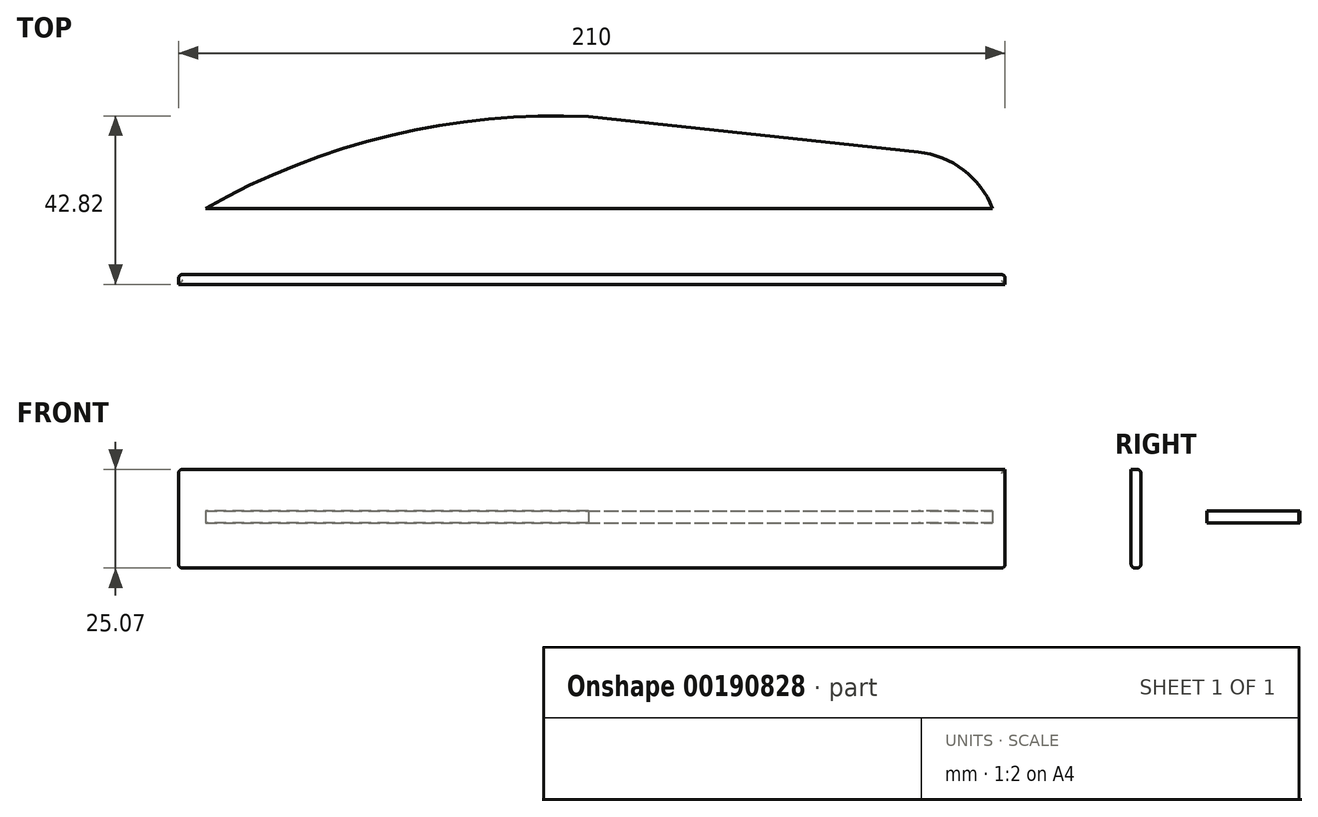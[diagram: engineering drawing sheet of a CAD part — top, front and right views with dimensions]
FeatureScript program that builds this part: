
annotation { "Feature Type Name" : "Feature", "Feature Type Description" : "" }
export const myFeature = defineFeature(function(context is Context, id is Id, definition is map)
    precondition{}
    {
        {
            var Q0;
            Q0=qCreatedBy(makeId("Top.planeOp"),FACE);
            var sketch = newSketch(context, id + "F0", { "sketchPlane" : qUnion([Q0])});
            skLineSegment(sketch, "E0", {"start": v(-82.54, 16.8) * mm, "end": v(117.46, 16.8) * mm});
            skArc(sketch, "E1", {"start": v(14.74, 40.14) * mm, "mid": v(-35.55, 35.33) * mm, "end": v(-82.54, 16.8) * mm});
            skLineSegment(sketch, "E2", {"start": v(14.74, 40.14) * mm, "end": v(98.58, 31.13) * mm});
            skArc(sketch, "E3", {"start": v(117.46, 16.8) * mm, "mid": v(110.01, 26.59) * mm, "end": v(98.58, 31.13) * mm});
            skSolve(sketch);
        }
        {
            var Q0;
            Q0=makeQuery(id+"F0.imprint","IMPRINT",FACE,{"disambiguationData":[TD([[makeQuery(id+"F0.imprint","IMPRINT",EDGE,{"derivedFrom":sQuery(id+"F0.wireOp",EDGE,"E0")}),1.0]])]});
            extrude(context, id + "F1", {"entities" : qUnion([Q0]), "depth" : 3 * mm});
        }
        {
            var Q0;
            Q0=qCreatedBy(makeId("Front.planeOp"),FACE);
            var sketch = newSketch(context, id + "F2", { "sketchPlane" : qUnion([Q0])});
            skLineSegment(sketch, "E4.bottom", {"start": v(-89.37, 13.57) * mm, "end": v(120.63, 13.57) * mm});
            skLineSegment(sketch, "E4.top", {"start": v(-89.37, -11.5) * mm, "end": v(120.63, -11.5) * mm});
            skLineSegment(sketch, "E4.left", {"start": v(-89.37, 13.57) * mm, "end": v(-89.37, -11.5) * mm});
            skLineSegment(sketch, "E4.right", {"start": v(120.63, 13.57) * mm, "end": v(120.63, -11.5) * mm});
            skSolve(sketch);
        }
        {
            var Q0;
            Q0=makeQuery(id+"F2.imprint","IMPRINT",FACE,{"disambiguationData":[TD([[makeQuery(id+"F2.imprint","IMPRINT",EDGE,{"derivedFrom":sQuery(id+"F2.wireOp",EDGE,"E4.bottom")}),-1.0]])]});
            extrude(context, id + "F3", {"entities" : qUnion([Q0]), "depth" : 2.5 * mm});
        }
        {
            var Q0;
            Q0=makeQuery(id+"F3.opExtrude","SWEPT_EDGE",EDGE,{"disambiguationData":[OSD([sQuery(id+"F2.wireOp",EDGE,"E4.bottom"),sQuery(id+"F2.wireOp",EDGE,"E4.left")])]});
            var Q1;
            Q1=makeQuery(id+"F3.opExtrude","CAP_EDGE",EDGE,{"disambiguationData":[OSD([sQuery(id+"F2.wireOp",EDGE,"E4.bottom")])],"isStart":true});
            var Q2;
            Q2=makeQuery(id+"F3.opExtrude","CAP_EDGE",EDGE,{"disambiguationData":[OSD([sQuery(id+"F2.wireOp",EDGE,"E4.right")])],"isStart":true});
            var Q3;
            Q3=makeQuery(id+"F3.opExtrude","SWEPT_EDGE",EDGE,{"disambiguationData":[OSD([sQuery(id+"F2.wireOp",EDGE,"E4.top"),sQuery(id+"F2.wireOp",EDGE,"E4.right")])]});
            var Q4;
            Q4=makeQuery(id+"F3.opExtrude","CAP_EDGE",EDGE,{"disambiguationData":[OSD([sQuery(id+"F2.wireOp",EDGE,"E4.top")])],"isStart":true});
            var Q5;
            Q5=makeQuery(id+"F3.opExtrude","CAP_EDGE",EDGE,{"disambiguationData":[OSD([sQuery(id+"F2.wireOp",EDGE,"E4.top")])],"isStart":false});
            var Q6;
            Q6=makeQuery(id+"F3.opExtrude","SWEPT_EDGE",EDGE,{"disambiguationData":[OSD([sQuery(id+"F2.wireOp",EDGE,"E4.top"),sQuery(id+"F2.wireOp",EDGE,"E4.left")])]});
            var Q7;
            Q7=makeQuery(id+"F3.opExtrude","CAP_EDGE",EDGE,{"disambiguationData":[OSD([sQuery(id+"F2.wireOp",EDGE,"E4.left")])],"isStart":true});
            fillet(context, id + "F4", {"entities" : qUnion([Q0, Q1, Q2, Q3, Q4, Q5, Q6, Q7]), "radius" : 1 * mm, "tangentPropagation" : true, "allowEdgeOverflow" : false});
        }
    });
